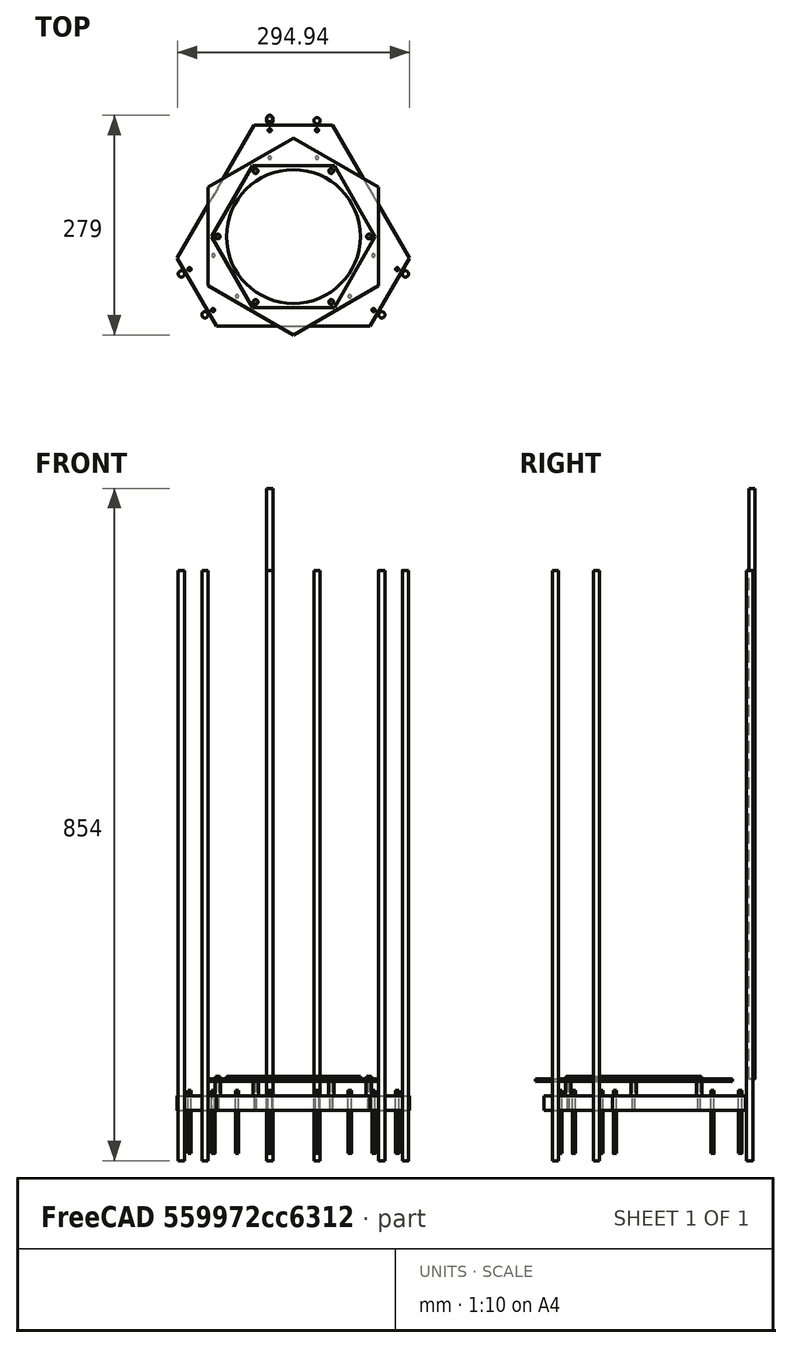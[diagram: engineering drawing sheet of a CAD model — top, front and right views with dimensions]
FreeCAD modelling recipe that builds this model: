
FCSTD DOCUMENT  (FreeCAD 0.16R6703 (Git))
Label: delta_ns
License: All rights reserved
LicenseURL: http://en.wikipedia.org/wiki/All_rights_reserved
objects: Part::Part2DObjectPython×8, App::FeaturePython×8, Part::Cylinder×6, Part::FeaturePython×6, Sketcher::SketchObject×5, PartDesign::Pad×3, Part::Feature×3, Part::MultiFuse×2, App::DocumentObjectGroup×2, Mesh::Feature×1, Part::Prism×1
note: 37 computed .brp shape members not serialized (recipe doc carries the construction recipe); baked Part::Feature solids carry a one-line shape summary decoded from their .brp

FEATURE [Mesh::Feature] motor_end
FEATURE [Part::Cylinder] Cylinder
  Angle = 360
  Height = 750
  Placement = pos=(-30,150,0) rot=(0,0,1;0rad)
  Radius = 4
FEATURE [Part::Cylinder] Cylinder001  label="print_glass"
  Angle = 360
  Height = 3
  Radius = 85
  expr: Radius = 17cm / 2
FEATURE [Part::Prism] Prism
  Circumradius = 125
  Height = 3
  Placement = pos=(0,0,-3) rot=(0,0,1;0.523599rad)
  Polygon = 6
FEATURE [Part::Part2DObjectPython] Circle001  # Draft 2D object (typed FeaturePython)
  FirstAngle = 0
  LastAngle = 0
  MakeFace = false
  Placement = pos=(0,0,3) rot=(0,0,1;0rad)
  Radius = 150
FEATURE [Part::Part2DObjectPython] Circle  # Draft 2D object (typed FeaturePython)
  FirstAngle = 0
  LastAngle = 0
  MakeFace = true
  Placement = pos=(-123.944,-0.717884,0) rot=(0,0,1;0rad)
  Radius = 15
FEATURE [Sketcher::SketchObject] Sketch
  expr: Constraints[9] = 19.2cm / 2
  sketch-geometry (12):
    g0: Circle CenterX=0 CenterY=0 CenterZ=0 NormalX=0 NormalY=0 NormalZ=1 Radius=150
    g1: Circle [constr] CenterX=-30 CenterY=146.969 CenterZ=0 NormalX=0 NormalY=0 NormalZ=1 Radius=4
    g2: Circle [constr] CenterX=30 CenterY=146.969 CenterZ=0 NormalX=0 NormalY=0 NormalZ=1 Radius=4
    g3: Circle CenterX=0 CenterY=0 CenterZ=0 NormalX=0 NormalY=0 NormalZ=1 Radius=96
    g4: LineSegment [constr] StartX=-30 StartY=134.969 StartZ=0 EndX=30 EndY=134.969 EndZ=0
    g5: LineSegment [constr] StartX=30 StartY=134.969 StartZ=0 EndX=30 EndY=99.9694 EndZ=0
    g6: LineSegment [constr] StartX=30 StartY=99.9694 StartZ=0 EndX=-30 EndY=99.9694 EndZ=0
    g7: LineSegment [constr] StartX=-30 StartY=99.9694 StartZ=0 EndX=-30 EndY=134.969 EndZ=0
    g8: Circle CenterX=-30 CenterY=134.969 CenterZ=0 NormalX=0 NormalY=0 NormalZ=1 Radius=2.2
    g9: Circle CenterX=-30 CenterY=99.9694 CenterZ=0 NormalX=0 NormalY=0 NormalZ=1 Radius=2.2
    g10: Circle CenterX=30 CenterY=99.9694 CenterZ=0 NormalX=0 NormalY=0 NormalZ=1 Radius=2.2
    g11: Circle CenterX=30 CenterY=134.969 CenterZ=0 NormalX=0 NormalY=0 NormalZ=1 Radius=2.2
  constraints (29):
    c: Coincident(g0,g-1)
    c: Radius(g0) = 150
    c: PointOnObject(g1,g0)
    c: PointOnObject(g2,g0)
    c: Radius(g1) = 4
    c: Equal(g1,g2)
    c: Symmetric(g1,g2,g-2)
    c: Distance(g1,g2) = 60
    c: Coincident(g3,g-1)
    c: Radius(g3) = 96
    c: Coincident(g4,g5)
    c: Coincident(g5,g6)
    c: Coincident(g6,g7)
    c: Coincident(g7,g4)
    c: Horizontal(g6)
    c: Vertical(g5)
    c: Vertical(g7)
    c: DistanceY(g4,g1) = 12
    c: DistanceY(g5,g5) = 35
    c: Coincident(g8,g4)
    c: Coincident(g9,g6)
    c: Coincident(g10,g5)
    c: Coincident(g11,g4)
    c: Symmetric(g4,g4,g-2)
    c: DistanceX(g6,g6) = 60
    c: Radius(g8) = 2.2
    c: Equal(g8,g9)
    c: Equal(g8,g11)
    c: Equal(g8,g10)
FEATURE [Sketcher::SketchObject] Sketch001
  sketch-geometry (4):
    g0: LineSegment StartX=-30 StartY=138.069 StartZ=0 EndX=30 EndY=138.069 EndZ=0
    g1: LineSegment StartX=30 StartY=138.069 StartZ=0 EndX=30 EndY=102.069 EndZ=0
    g2: LineSegment StartX=30 StartY=102.069 StartZ=0 EndX=-30 EndY=102.069 EndZ=0
    g3: LineSegment StartX=-30 StartY=102.069 StartZ=0 EndX=-30 EndY=138.069 EndZ=0
  constraints (11):
    c: Coincident(g0,g1)
    c: Coincident(g1,g2)
    c: Coincident(g2,g3)
    c: Coincident(g3,g0)
    c: Horizontal(g0)
    c: Horizontal(g2)
    c: Vertical(g1)
    c: Vertical(g3)
    c: Symmetric(g0,g0,g-2)
    c: DistanceX(g0,g0) = 60
    c: DistanceY(g3,g3) = 36
FEATURE [Sketcher::SketchObject] Sketch002
  Placement = pos=(0,0,-22) rot=(0,0,1;0rad)
  sketch-geometry (7):
    g0: LineSegment StartX=50 StartY=141.421 StartZ=0 EndX=-50 EndY=141.421 EndZ=0
    g1: LineSegment StartX=-50 StartY=141.421 StartZ=0 EndX=-147.474 EndY=-27.4094 EndZ=0
    g2: LineSegment StartX=-147.474 StartY=-27.4094 StartZ=0 EndX=-97.4745 EndY=-114.012 EndZ=0
    g3: LineSegment StartX=-97.4745 StartY=-114.012 StartZ=0 EndX=97.4745 EndY=-114.012 EndZ=0
    g4: LineSegment StartX=97.4745 StartY=-114.012 StartZ=0 EndX=147.474 EndY=-27.4094 EndZ=0
    g5: LineSegment StartX=147.474 StartY=-27.4094 StartZ=0 EndX=50 EndY=141.421 EndZ=0
    g6: Circle [constr] CenterX=0 CenterY=0 CenterZ=0 NormalX=0 NormalY=0 NormalZ=1 Radius=150
  constraints (20):
    c: Coincident(g0,g1)
    c: Coincident(g1,g2)
    c: Coincident(g2,g3)
    c: Coincident(g3,g4)
    c: Coincident(g4,g5)
    c: Coincident(g5,g0)
    c: PointOnObject(g0,g6)
    c: PointOnObject(g1,g6)
    c: PointOnObject(g2,g6)
    c: PointOnObject(g3,g6)
    c: PointOnObject(g4,g6)
    c: PointOnObject(g5,g6)
    c: Coincident(g6,g-1)
    c: Perpendicular(g-2,g0)
    c: Equal(g3,g1)
    c: Equal(g1,g5)
    c: Equal(g0,g2)
    c: Equal(g2,g4)
    c: Radius(g6) = 150
    c: Distance(g0) = 100
FEATURE [Sketcher::SketchObject] Sketch003
  sketch-geometry (7):
    g0: LineSegment StartX=103.923 StartY=0 StartZ=0 EndX=51.9615 EndY=90 EndZ=0
    g1: LineSegment StartX=51.9615 StartY=90 StartZ=0 EndX=-51.9615 EndY=90 EndZ=0
    g2: LineSegment StartX=-51.9615 StartY=90 StartZ=0 EndX=-103.923 EndY=0 EndZ=0
    g3: LineSegment StartX=-103.923 StartY=0 StartZ=0 EndX=-51.9615 EndY=-90 EndZ=0
    g4: LineSegment StartX=-51.9615 StartY=-90 StartZ=0 EndX=51.9615 EndY=-90 EndZ=0
    g5: LineSegment StartX=51.9615 StartY=-90 StartZ=0 EndX=103.923 EndY=0 EndZ=0
    g6: Circle [constr] CenterX=0 CenterY=0 CenterZ=0 NormalX=0 NormalY=0 NormalZ=1 Radius=103.923
  constraints (16):
    c: Coincident(g0,g1)
    c: Coincident(g1,g2)
    c: Coincident(g2,g3)
    c: Coincident(g3,g4)
    c: Coincident(g4,g5)
    c: Coincident(g5,g0)
    c: Equal(g0, g1-g5) x5
    c: PointOnObject(g0,g6)
    c: PointOnObject(g1,g6)
    c: PointOnObject(g2,g6)
    c: PointOnObject(g3,g6)
    c: PointOnObject(g4,g6)
    c: PointOnObject(g5,g6)
    c: Coincident(g6,g-1)
    c: Distance(g1,g0) = 180
    c: Perpendicular(g-2,g1)
FEATURE [PartDesign::Pad] Pad  label="Bed_Heater"
  Length = 1.7
  Length2 = 100
  Reversed = true
  Sketch = -> Sketch003
  Type = 0
FEATURE [Part::Cylinder] Cylinder002  label="Cylinder001"
  Angle = 360
  Height = 40
  Placement = pos=(96,0,-10) rot=(0,0,1;0rad)
  Radius = 1.5
  expr: Placement.Base.x = 19.2cm / 2
FEATURE [Part::Cylinder] Cylinder003  label="Cylinder002"
  Angle = 360
  Height = 3
  Placement = pos=(96,0,30) rot=(0,0,1;0rad)
  Radius = 3
FEATURE [Part::MultiFuse] Fusion
  Placement = pos=(0,0,-30) rot=(0,0,1;0rad)
  Shapes = -> [Cylinder002,Cylinder003]
FEATURE [Part::FeaturePython] Array  label="bed_screws"  # Draft array (typed FeaturePython)
  Angle = 360
  ArrayType = 1
  Axis = (0,0,1)
  Base = -> Fusion
  Center = (0,0,0)
  Fuse = false
  IntervalAxis = (0,0,0)
  IntervalX = (1,0,0)
  IntervalY = (0,1,0)
  IntervalZ = (0,0,0)
  NumberPolar = 6
  NumberX = 2
  NumberY = 2
  NumberZ = 1
FEATURE [Part::Cylinder] Cylinder004  label="Cylinder003"
  Angle = 360
  Height = 20
  Placement = pos=(96,0,-22) rot=(0,0,1;0rad)
  Radius = 3.5
FEATURE [Part::FeaturePython] Array001  label="bed_springs"  # Draft array (typed FeaturePython)
  Angle = 360
  ArrayType = 1
  Axis = (0,0,1)
  Base = -> Cylinder004
  Center = (0,0,0)
  Fuse = false
  IntervalAxis = (0,0,0)
  IntervalX = (1,0,0)
  IntervalY = (0,1,0)
  IntervalZ = (0,0,0)
  NumberPolar = 6
  NumberX = 2
  NumberY = 2
  NumberZ = 1
FEATURE [PartDesign::Pad] Pad001
  Length = 18
  Length2 = 100
  Placement = pos=(0,0,-22) rot=(0,0,1;0rad)
  Reversed = true
  Sketch = -> Sketch002
  Type = 0
FEATURE [Sketcher::SketchObject] Sketch004
  Placement = pos=(0,0,-15) rot=(0,0,1;0rad)
  sketch-geometry (9):
    g0: LineSegment [constr] StartX=-30 StartY=135 StartZ=0 EndX=30 EndY=135 EndZ=0
    g1: LineSegment [constr] StartX=30 StartY=135 StartZ=0 EndX=30 EndY=100 EndZ=0
    g2: LineSegment [constr] StartX=30 StartY=100 StartZ=0 EndX=-30 EndY=100 EndZ=0
    g3: LineSegment [constr] StartX=-30 StartY=100 StartZ=0 EndX=-30 EndY=135 EndZ=0
    g4: Circle CenterX=-30 CenterY=135 CenterZ=0 NormalX=0 NormalY=0 NormalZ=1 Radius=2
    g5: Circle CenterX=-30 CenterY=100 CenterZ=0 NormalX=0 NormalY=0 NormalZ=1 Radius=2
    g6: Circle CenterX=30 CenterY=135 CenterZ=0 NormalX=0 NormalY=0 NormalZ=1 Radius=2
    g7: Circle CenterX=30 CenterY=100 CenterZ=0 NormalX=0 NormalY=0 NormalZ=1 Radius=2
    g8: Circle [constr] CenterX=-30 CenterY=135 CenterZ=0 NormalX=0 NormalY=0 NormalZ=1 Radius=5
  constraints (22):
    c: Coincident(g0,g1)
    c: Coincident(g1,g2)
    c: Coincident(g2,g3)
    c: Coincident(g3,g0)
    c: Horizontal(g0)
    c: Horizontal(g2)
    c: Vertical(g1)
    c: Vertical(g3)
    c: Symmetric(g0,g0,g-2)
    c: DistanceX(g0,g0) = 60
    c: DistanceY(g-1,g0) = 135
    c: DistanceY(g1,g1) = 35
    c: Coincident(g4,g0)
    c: Coincident(g5,g2)
    c: Coincident(g6,g0)
    c: Coincident(g7,g1)
    c: Radius(g4) = 2
    c: Equal(g4,g5)
    c: Equal(g4,g7)
    c: Equal(g4,g6)
    c: Coincident(g8,g0)
    c: Radius(g8) = 5
FEATURE [PartDesign::Pad] Pad002
  Length = 80
  Length2 = 100
  Placement = pos=(0,0,-15) rot=(0,0,1;0rad)
  Reversed = true
  Sketch = -> Sketch004
  Type = 0
FEATURE [Part::FeaturePython] Array002  # Draft array (typed FeaturePython)
  Angle = 360
  ArrayType = 1
  Axis = (0,0,1)
  Base = -> Pad002
  Center = (0,0,0)
  Fuse = false
  IntervalAxis = (0,0,0)
  IntervalX = (1,0,0)
  IntervalY = (0,1,0)
  IntervalZ = (0,0,0)
  NumberPolar = 3
  NumberX = 2
  NumberY = 2
  NumberZ = 1
FEATURE [App::DocumentObjectGroup] Group  label="Bed"
  Group = -> [Array001,Array,Pad,Cylinder001]
FEATURE [Part::Cylinder] Cylinder005  label="Cylinder004"
  Angle = 360
  Height = 750
  Placement = pos=(-30,146.969,0) rot=(0,0,1;0rad)
  Radius = 4
FEATURE [Part::FeaturePython] Clone  label="Clone of Cylinder004"  # Draft clone (typed FeaturePython)
  Objects = -> [Cylinder005]
  Placement = pos=(30,146.969,0) rot=(0,0,1;0rad)
  Scale = (1,1,1)
FEATURE [Part::MultiFuse] Fusion001
  Placement = pos=(0,0,-104) rot=(0,0,1;0rad)
  Shapes = -> [Clone,Cylinder005]
FEATURE [Part::FeaturePython] Array004  # Draft array (typed FeaturePython)
  Angle = 360
  ArrayType = 1
  Axis = (0,0,1)
  Base = -> Fusion001
  Center = (0,0,0)
  Fuse = false
  IntervalAxis = (0,0,0)
  IntervalX = (1,0,0)
  IntervalY = (0,1,0)
  IntervalZ = (0,0,0)
  NumberPolar = 3
  NumberX = 2
  NumberY = 2
  NumberZ = 1
FEATURE [Part::Feature] motor_end_v1001
  shape: bbox 72 x 64 x 44 mm, 9228 faces, 0 solids (baked)
FEATURE [Part::Feature] Part__Mirroring003  label="motor_end_v1002 (Mirror #1)001"
  Placement = pos=(0,147,-40) rot=(0,0,1;3.14159rad)
  shape: bbox 72 x 64 x 44 mm, 3977 faces, 0 solids (baked)
FEATURE [Part::FeaturePython] Array005  # Draft array (typed FeaturePython)
  Angle = 360
  ArrayType = 1
  Axis = (0,0,1)
  Base = -> Part__Mirroring003
  Center = (0,0,0)
  Fuse = false
  IntervalAxis = (0,0,0)
  IntervalX = (1,0,0)
  IntervalY = (0,1,0)
  IntervalZ = (0,0,0)
  NumberPolar = 3
  NumberX = 2
  NumberY = 2
  NumberZ = 1
FEATURE [Part::Feature] idler_end_v3001001  label="idler_end_v3002"
  Placement = pos=(0,0,50) rot=(0,0,1;0rad)
  shape: bbox 72 x 28 x 39 mm, 4986 faces, 0 solids (baked)
FEATURE [App::FeaturePython] Dimension  # Draft dimension (typed FeaturePython)
  Dimline = (19,138,0)
  Direction = (0,0,0)
  Distance = 60
  End = (30,135,0)
  Normal = (0,0,1)
  Start = (-30,135,0)
FEATURE [App::FeaturePython] Dimension001  # Draft dimension (typed FeaturePython)
  Dimline = (-35,99,0)
  Direction = (0,0,0)
  Distance = 35
  End = (-30,99.9694,0)
  Normal = (0,0,1)
  Start = (-30,134.969,0)
FEATURE [App::FeaturePython] Dimension002  # Draft dimension (typed FeaturePython)
  Dimline = (-35,140,0)
  Direction = (0,0,0)
  Distance = 12
  End = (-30,146.969,0)
  Normal = (0,0,1)
  Start = (-30,134.969,0)
FEATURE [App::FeaturePython] Dimension003  # Draft dimension (typed FeaturePython)
  Dimline = (43.992,157.349,0)
  Direction = (0,0,0)
  Distance = 100
  End = (50,141.421,0)
  Normal = (0,0,1)
  Start = (-50,141.421,0)
FEATURE [App::FeaturePython] Dimension004  # Draft dimension (typed FeaturePython)
  Dimline = (23.3141,114.108,0)
  Direction = (0,0,0)
  Distance = 150
  End = (0,0,0)
  Normal = (0,0,1)
  Start = (30,146.969,0)
FEATURE [App::FeaturePython] Dimension005  # Draft dimension (typed FeaturePython)
  Dimline = (0.0209096,-0.00426817,0)
  Direction = (0,0,0)
  Distance = 96.0142
  End = (0.0209096,-0.00426817,0)
  Normal = (0,0,1)
  Start = (-48,83.1384,0)
FEATURE [App::FeaturePython] Dimension006  # Draft dimension (typed FeaturePython)
  Dimline = (36.6474,85.6128,0)
  Direction = (0,0,0)
  Distance = 96
  End = (48,83.1384,0)
  Normal = (0,0,1)
  Start = (-48,83.1384,0)
FEATURE [App::FeaturePython] Dimension007  # Draft dimension (typed FeaturePython)
  Dimline = (153.762,-21.1219,0)
  Direction = (0,0,0)
  Distance = 194.949
  End = (147.474,-27.4094,0)
  Normal = (0,0,1)
  Start = (50,141.421,0)
FEATURE [Part::Part2DObjectPython] Line  # Draft 2D object (typed FeaturePython)
  ChamferSize = 0
  Closed = false
  End = (-24.9507,129.92,0)
  FilletRadius = 0
  Length = 7.14076
  MakeFace = true
  Points = (2) [(-30,134.969,0),(-24.9507,129.92,0)]
  Start = (-30,134.969,0)
  Subdivisions = 0
FEATURE [Part::Part2DObjectPython] Line001  # Draft 2D object (typed FeaturePython)
  ChamferSize = 0
  Closed = false
  End = (-24.7687,152.201,0)
  FilletRadius = 0
  Length = 7.39816
  MakeFace = true
  Points = (2) [(-30,146.969,0),(-24.7687,152.201,0)]
  Start = (-30,146.969,0)
  Subdivisions = 0
FEATURE [Part::Part2DObjectPython] Line002  # Draft 2D object (typed FeaturePython)
  ChamferSize = 0
  Closed = false
  End = (-55.5538,90.6922,0)
  FilletRadius = 0
  Length = 10.6826
  MakeFace = true
  Points = (2) [(-48,83.1384,0),(-55.5538,90.6922,0)]
  Start = (-48,83.1384,0)
  Subdivisions = 0
FEATURE [Part::Part2DObjectPython] ShapeString  # Draft 2D object (typed FeaturePython)
  FontFile = <path>
  Placement = pos=(-24.7687,152.201,0) rot=(0,0,1;0rad)
  Size = 0.5
  String = 8mm steel rod
  Tracking = 0
FEATURE [Part::Part2DObjectPython] ShapeString001  # Draft 2D object (typed FeaturePython)
  FontFile = <path>
  Placement = pos=(-24.9507,129.92,0) rot=(0,0,1;0rad)
  Size = 0.5
  String = M4 screw
  Tracking = 0
FEATURE [Part::Part2DObjectPython] ShapeString002  # Draft 2D object (typed FeaturePython)
  FontFile = <path>
  Placement = pos=(-55.5538,90.6922,0) rot=(0,0,1;0rad)
  Size = 0.5
  String = M3 screw
  Tracking = 0
FEATURE [App::DocumentObjectGroup] Group001  label="CNC_sketch"
  Group = -> [Dimension,Dimension001,Dimension002,Dimension003,Dimension004,Dimension005,Dimension006,Dimension007,Line,Line001,Line002,ShapeString,ShapeString001,ShapeString002,Sketch]
note: 3 file-system paths scrubbed to <path> (originals preserved in the JSON sidecar)
